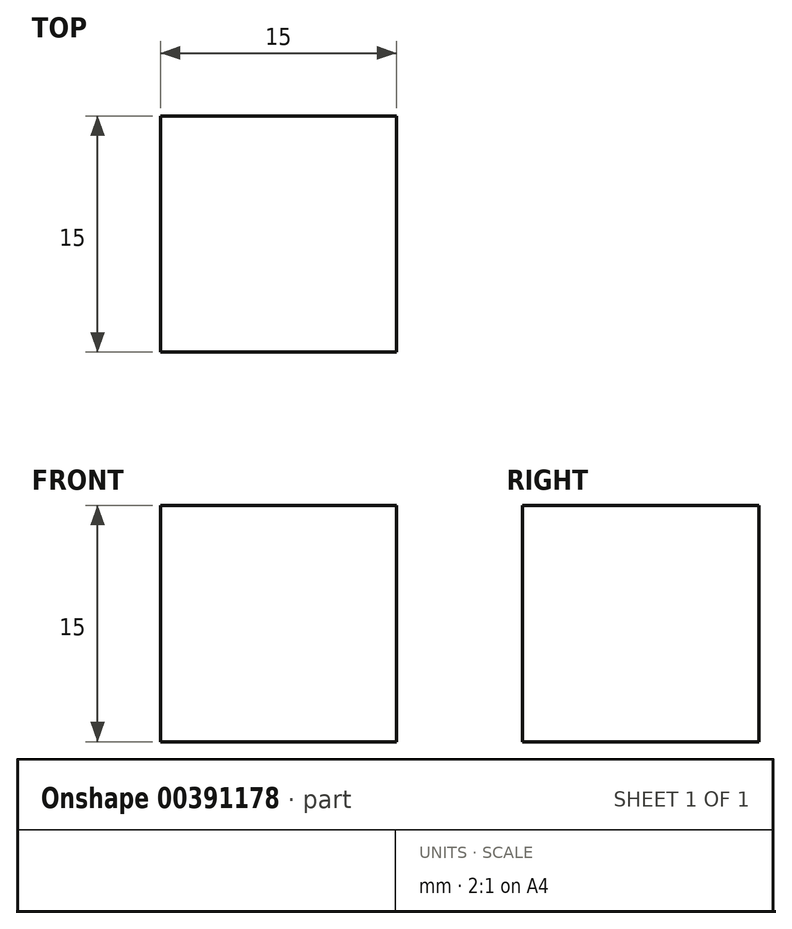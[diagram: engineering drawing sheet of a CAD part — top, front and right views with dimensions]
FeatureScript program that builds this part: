
annotation { "Feature Type Name" : "Feature", "Feature Type Description" : "" }
export const myFeature = defineFeature(function(context is Context, id is Id, definition is map)
    precondition{}
    {
        {
            var Q0;
            Q0=qCreatedBy(makeId("Front.planeOp"),FACE);
            var sketch = newSketch(context, id + "F0", { "sketchPlane" : qUnion([Q0])});
            skLineSegment(sketch, "E0.bottom", {"start": v(-7.5, 7.5) * mm, "end": v(7.5, 7.5) * mm});
            skLineSegment(sketch, "E0.top", {"start": v(-7.5, -7.5) * mm, "end": v(7.5, -7.5) * mm});
            skLineSegment(sketch, "E0.left", {"start": v(-7.5, 7.5) * mm, "end": v(-7.5, -7.5) * mm});
            skLineSegment(sketch, "E0.right", {"start": v(7.5, 7.5) * mm, "end": v(7.5, -7.5) * mm});
            skPoint(sketch, "E0.middle", {"position": v(0, 0) * mm});
            skSolve(sketch);
        }
        {
            var Q0;
            Q0=makeQuery(id+"F0.imprint","IMPRINT",FACE,{"disambiguationData":[TD([[makeQuery(id+"F0.imprint","IMPRINT",EDGE,{"derivedFrom":sQuery(id+"F0.wireOp",EDGE,"E0.bottom")}),-1.0]])]});
            extrude(context, id + "F1", {"entities" : qUnion([Q0]), "endBound" : BoundingType.SYMMETRIC, "depth" : 15 * mm});
        }
    });
